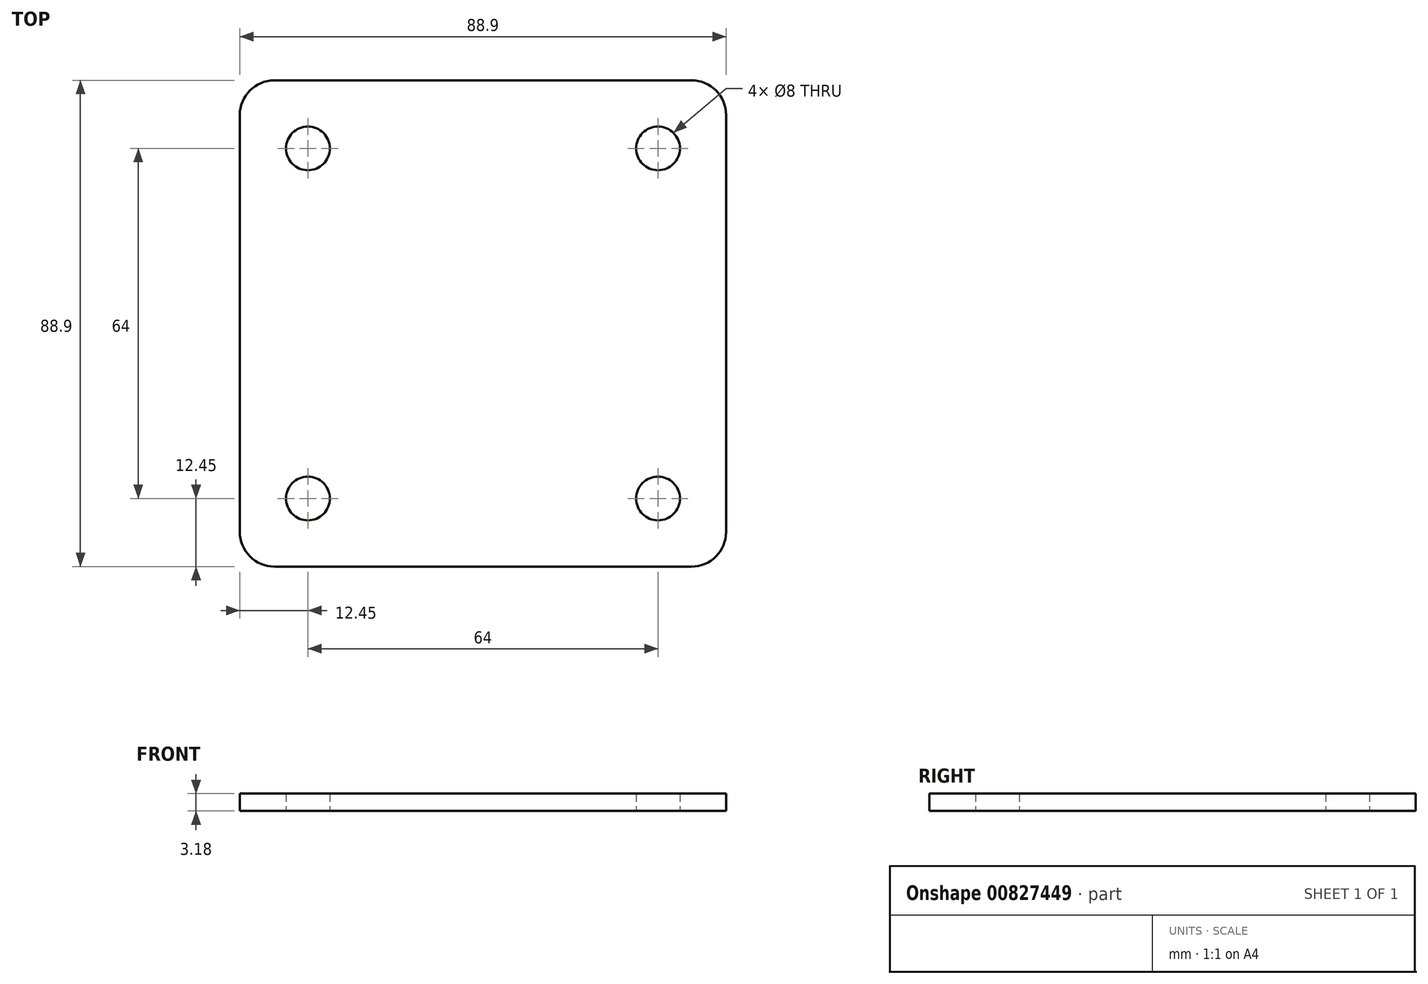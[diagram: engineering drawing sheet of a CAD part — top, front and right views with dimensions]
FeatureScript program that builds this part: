
annotation { "Feature Type Name" : "Feature", "Feature Type Description" : "" }
export const myFeature = defineFeature(function(context is Context, id is Id, definition is map)
    precondition{}
    {
        {
            var Q0;
            Q0=qCreatedBy(makeId("Top.planeOp"),FACE);
            var sketch = newSketch(context, id + "F0", { "sketchPlane" : qUnion([Q0])});
            skLineSegment(sketch, "E0.bottom", {"start": v(0, 0) * mm, "end": v(-88.9, 0) * mm});
            skLineSegment(sketch, "E0.top", {"start": v(0, -88.9) * mm, "end": v(-88.9, -88.9) * mm});
            skLineSegment(sketch, "E0.left", {"start": v(0, 0) * mm, "end": v(0, -88.9) * mm});
            skLineSegment(sketch, "E0.right", {"start": v(-88.9, 0) * mm, "end": v(-88.9, -88.9) * mm});
            skCircle(sketch, "E1", {"center": v(-12.45, -12.45) * mm, "radius": 4 * mm});
            skCircle(sketch, "E2", {"center": v(-76.45, -76.45) * mm, "radius": 4 * mm});
            skCircle(sketch, "E3", {"center": v(-76.45, -12.45) * mm, "radius": 4 * mm});
            skCircle(sketch, "E4", {"center": v(-12.45, -76.45) * mm, "radius": 4 * mm});
            skLineSegment(sketch, "E5", {"start": v(0, 0) * mm, "end": v(-88.9, -88.9) * mm, "construction": true});
            skLineSegment(sketch, "E6", {"start": v(-88.9, 0) * mm, "end": v(0, -88.9) * mm, "construction": true});
            skSolve(sketch);
        }
        {
            var Q0;
            Q0=makeQuery(id+"F0.imprint","IMPRINT",FACE,{"disambiguationData":[TD([[makeQuery(id+"F0.imprint","IMPRINT",EDGE,{"derivedFrom":sQuery(id+"F0.wireOp",EDGE,"E0.bottom")}),1.0]])]});
            extrude(context, id + "F1", {"entities" : qUnion([Q0]), "depth" : 3.17 * mm, "offsetDistance" : 25.4 * mm});
        }
        {
            var Q0;
            Q0=makeQuery(id+"F1.opExtrude","SWEPT_EDGE",EDGE,{"disambiguationData":[OSD([sQuery(id+"F0.wireOp",EDGE,"E0.bottom"),sQuery(id+"F0.wireOp",EDGE,"E0.right")])]});
            var Q1;
            Q1=makeQuery(id+"F1.opExtrude","SWEPT_EDGE",EDGE,{"disambiguationData":[OSD([sQuery(id+"F0.wireOp",EDGE,"E0.top"),sQuery(id+"F0.wireOp",EDGE,"E0.right")])]});
            var Q2;
            Q2=makeQuery(id+"F1.opExtrude","SWEPT_EDGE",EDGE,{"disambiguationData":[OSD([sQuery(id+"F0.wireOp",EDGE,"E0.top"),sQuery(id+"F0.wireOp",EDGE,"E0.left")])]});
            var Q3;
            Q3=makeQuery(id+"F1.opExtrude","SWEPT_EDGE",EDGE,{"disambiguationData":[OSD([sQuery(id+"F0.wireOp",EDGE,"E0.bottom"),sQuery(id+"F0.wireOp",EDGE,"E0.left")])]});
            fillet(context, id + "F2", {"entities" : qUnion([Q0, Q1, Q2, Q3]), "radius" : 6.35 * mm, "tangentPropagation" : true, "allowEdgeOverflow" : false});
        }
    });
